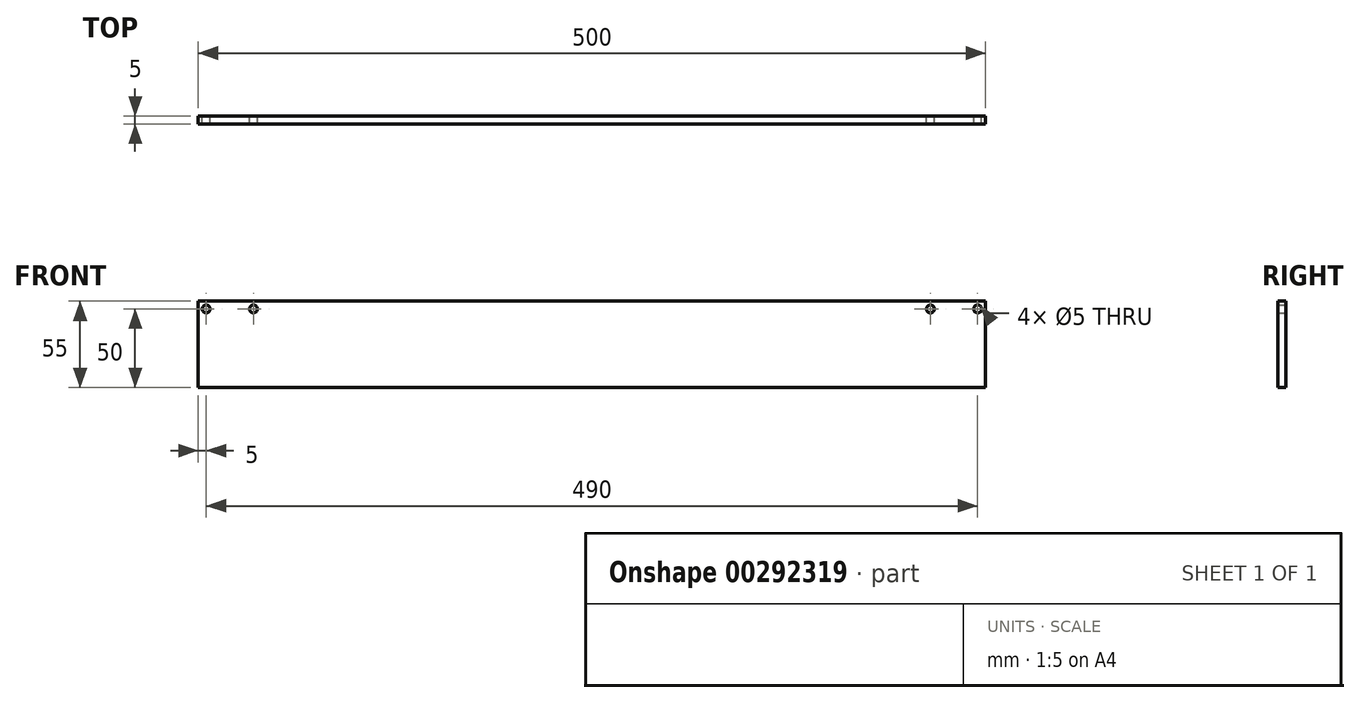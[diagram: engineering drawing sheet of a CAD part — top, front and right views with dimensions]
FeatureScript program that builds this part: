
annotation { "Feature Type Name" : "Feature", "Feature Type Description" : "" }
export const myFeature = defineFeature(function(context is Context, id is Id, definition is map)
    precondition{}
    {
        {
            var Q0;
            Q0=qCreatedBy(makeId("Front.planeOp"),FACE);
            var sketch = newSketch(context, id + "F0", { "sketchPlane" : qUnion([Q0])});
            skLineSegment(sketch, "E0.bottom", {"start": v(250, -27.5) * mm, "end": v(-250, -27.5) * mm});
            skLineSegment(sketch, "E0.top", {"start": v(250, 27.5) * mm, "end": v(-250, 27.5) * mm});
            skLineSegment(sketch, "E0.left", {"start": v(250, -27.5) * mm, "end": v(250, 27.5) * mm});
            skLineSegment(sketch, "E0.right", {"start": v(-250, -27.5) * mm, "end": v(-250, 27.5) * mm});
            skPoint(sketch, "E0.middle", {"position": v(0, 0) * mm});
            skCircle(sketch, "E1", {"center": v(-245, 22.5) * mm, "radius": 2.5 * mm});
            skCircle(sketch, "E2", {"center": v(-215, 22.5) * mm, "radius": 2.5 * mm});
            skLineSegment(sketch, "E3.MirrorCS", {"start": v(-250, 27.5) * mm, "end": v(250, 27.5) * mm});
            skCircle(sketch, "E4.MirrorC", {"center": v(215, 22.5) * mm, "radius": 2.5 * mm});
            skCircle(sketch, "E5.MirrorC", {"center": v(245, 22.5) * mm, "radius": 2.5 * mm});
            skSolve(sketch);
        }
        {
            var Q0;
            Q0 = qSketchRegion(id + "F0", true);
            extrude(context, id + "F1", {"entities" : qUnion([Q0]), "endBound" : BoundingType.SYMMETRIC, "depth" : 5 * mm});
        }
    });
